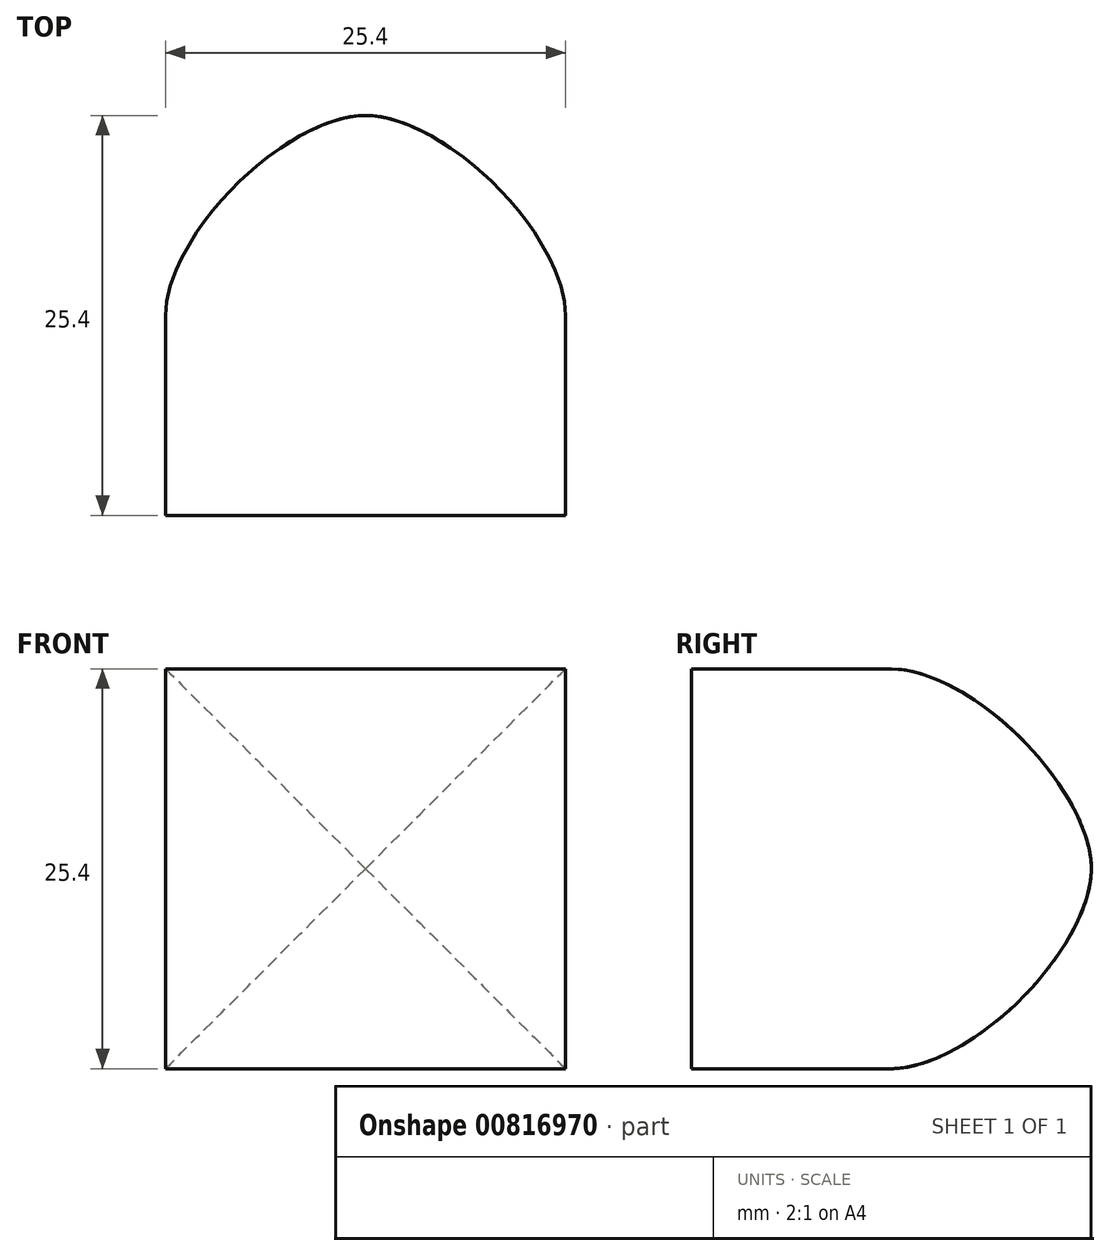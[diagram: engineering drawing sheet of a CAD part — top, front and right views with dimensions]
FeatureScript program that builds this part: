
annotation { "Feature Type Name" : "Feature", "Feature Type Description" : "" }
export const myFeature = defineFeature(function(context is Context, id is Id, definition is map)
    precondition{}
    {
        {
            var Q0;
            Q0=qCreatedBy(makeId("Top.planeOp"),FACE);
            var sketch = newSketch(context, id + "F0", { "sketchPlane" : qUnion([Q0])});
            skLineSegment(sketch, "E0", {"start": v(0, 25.4) * mm, "end": v(0, 0) * mm});
            skLineSegment(sketch, "E1", {"start": v(0, 25.4) * mm, "end": v(12.7, 25.4) * mm});
            skLineSegment(sketch, "E2", {"start": v(12.7, 25.4) * mm, "end": v(12.7, 0) * mm});
            skLineSegment(sketch, "E3", {"start": v(12.7, 0) * mm, "end": v(0, 0) * mm});
            skLineSegment(sketch, "E4.MirrorCS", {"start": v(-12.7, 0) * mm, "end": v(0, 0) * mm});
            skLineSegment(sketch, "E5.MirrorCS", {"start": v(0, 25.4) * mm, "end": v(-12.7, 25.4) * mm});
            skLineSegment(sketch, "E6.MirrorCS", {"start": v(-12.7, 25.4) * mm, "end": v(-12.7, 0) * mm});
            skSolve(sketch);
        }
        {
            var Q0;
            Q0=makeQuery(id+"F0.imprint","IMPRINT",FACE,{"disambiguationData":[TD([[makeQuery(id+"F0.imprint","IMPRINT",EDGE,{"derivedFrom":sQuery(id+"F0.wireOp",EDGE,"E0")}),-1.0]])]});
            var Q1;
            Q1=makeQuery(id+"F0.imprint","IMPRINT",FACE,{"disambiguationData":[TD([[makeQuery(id+"F0.imprint","IMPRINT",EDGE,{"derivedFrom":sQuery(id+"F0.wireOp",EDGE,"E0")}),1.0]])]});
            extrude(context, id + "F1", {"entities" : qUnion([Q0, Q1]), "depth" : 25.4 * mm, "offsetDistance" : 25.4 * mm});
        }
        {
            var Q0;
            Q0=makeQuery(id+"F1.opExtrude","SWEPT_FACE",FACE,{"disambiguationData":[OSD([sQuery(id+"F0.wireOp",EDGE,"E1"),sQuery(id+"F0.wireOp",EDGE,"E5.MirrorCS")])]});
            fillet(context, id + "F2", {"entities" : qUnion([Q0]), "radius" : 12.7 * mm, "rho" : 0.3, "crossSection" : FilletCrossSection.CONIC, "allowEdgeOverflow" : false});
        }
    });
